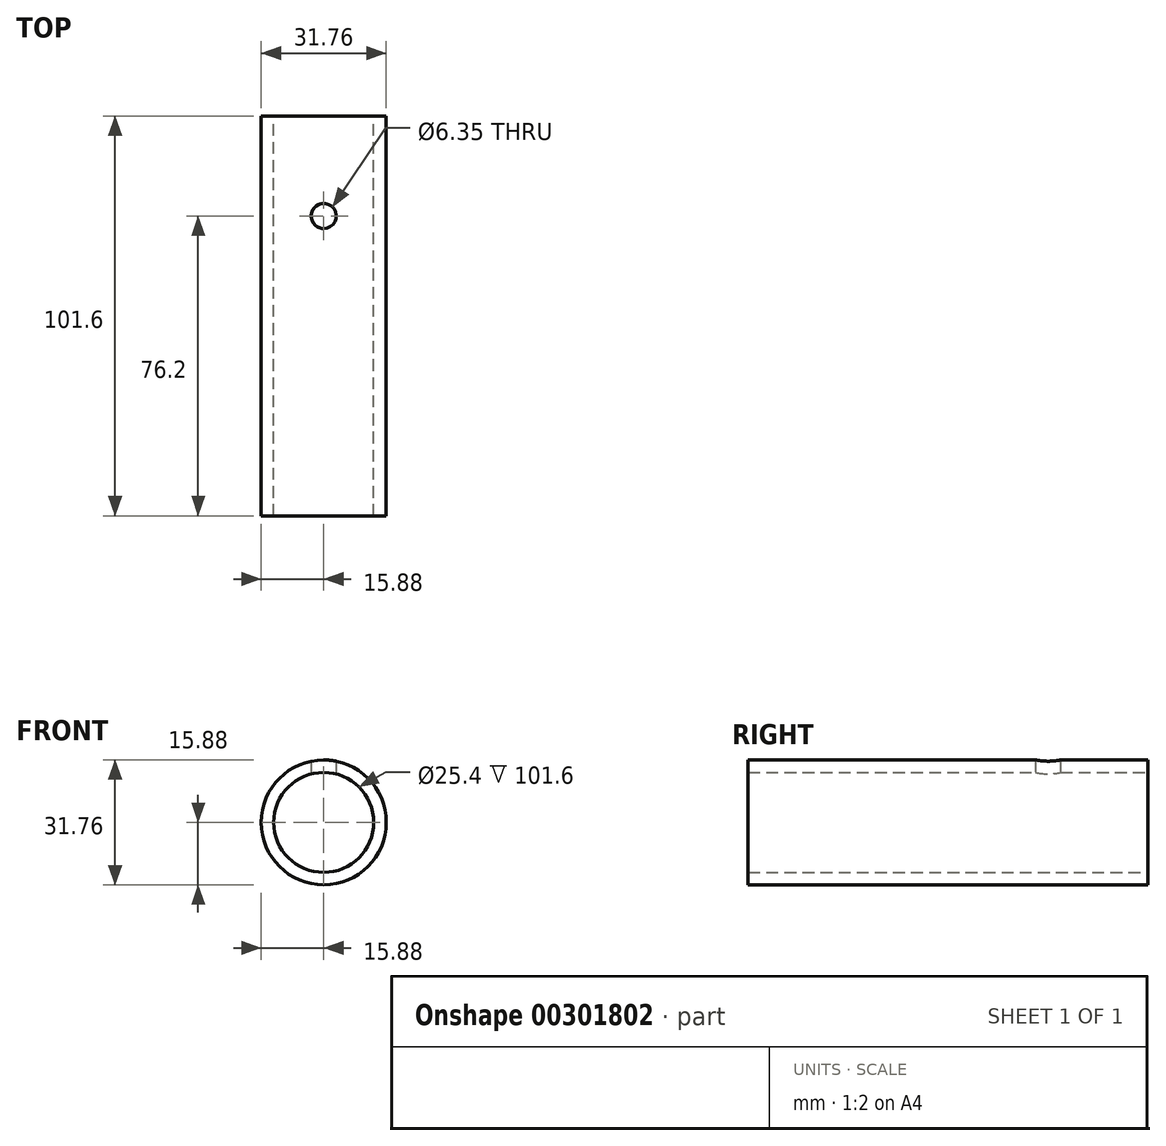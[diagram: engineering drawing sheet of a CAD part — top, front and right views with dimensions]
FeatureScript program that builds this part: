
annotation { "Feature Type Name" : "Feature", "Feature Type Description" : "" }
export const myFeature = defineFeature(function(context is Context, id is Id, definition is map)
    precondition{}
    {
        {
            var Q0;
            Q0=qCreatedBy(makeId("Front.planeOp"),FACE);
            var sketch = newSketch(context, id + "F0", { "sketchPlane" : qUnion([Q0])});
            skCircle(sketch, "E0", {"center": v(0, 0) * mm, "radius": 12.7 * mm});
            skCircle(sketch, "E1", {"center": v(0, 0) * mm, "radius": 15.88 * mm});
            skSolve(sketch);
        }
        {
            var Q0;
            Q0=makeQuery(id+"F0.imprint","IMPRINT",FACE,{"disambiguationData":[TD([[makeQuery(id+"F0.imprint","IMPRINT",EDGE,{"derivedFrom":sQuery(id+"F0.wireOp",EDGE,"E0")}),-1.0]])]});
            extrude(context, id + "F1", {"entities" : qUnion([Q0]), "depth" : 101.6 * mm});
        }
        {
            var Q0;
            Q0=qCreatedBy(makeId("Top.planeOp"),FACE);
            var sketch = newSketch(context, id + "F2", { "sketchPlane" : qUnion([Q0])});
            skLineSegment(sketch, "E2", {"start": v(15.88, 0) * mm, "end": v(15.88, -101.6) * mm});
            skLineSegment(sketch, "E3", {"start": v(-15.88, -101.6) * mm, "end": v(-15.88, 0) * mm});
            skCircle(sketch, "E4", {"center": v(0, -25.4) * mm, "radius": 3.18 * mm});
            skSolve(sketch);
        }
        {
            var Q0;
            Q0=makeQuery(id+"F2.imprint","IMPRINT",FACE,{"disambiguationData":[TD([[makeQuery(id+"F2.imprint","IMPRINT",EDGE,{"derivedFrom":sQuery(id+"F2.wireOp",EDGE,"E4")}),1.0]])]});
            extrude(context, id + "F3", {"entities" : qUnion([Q0]), "operationType" : NewBodyOperationType.REMOVE, "endBound" : BoundingType.THROUGH_ALL, "depth" : 25.4 * mm});
        }
    });
